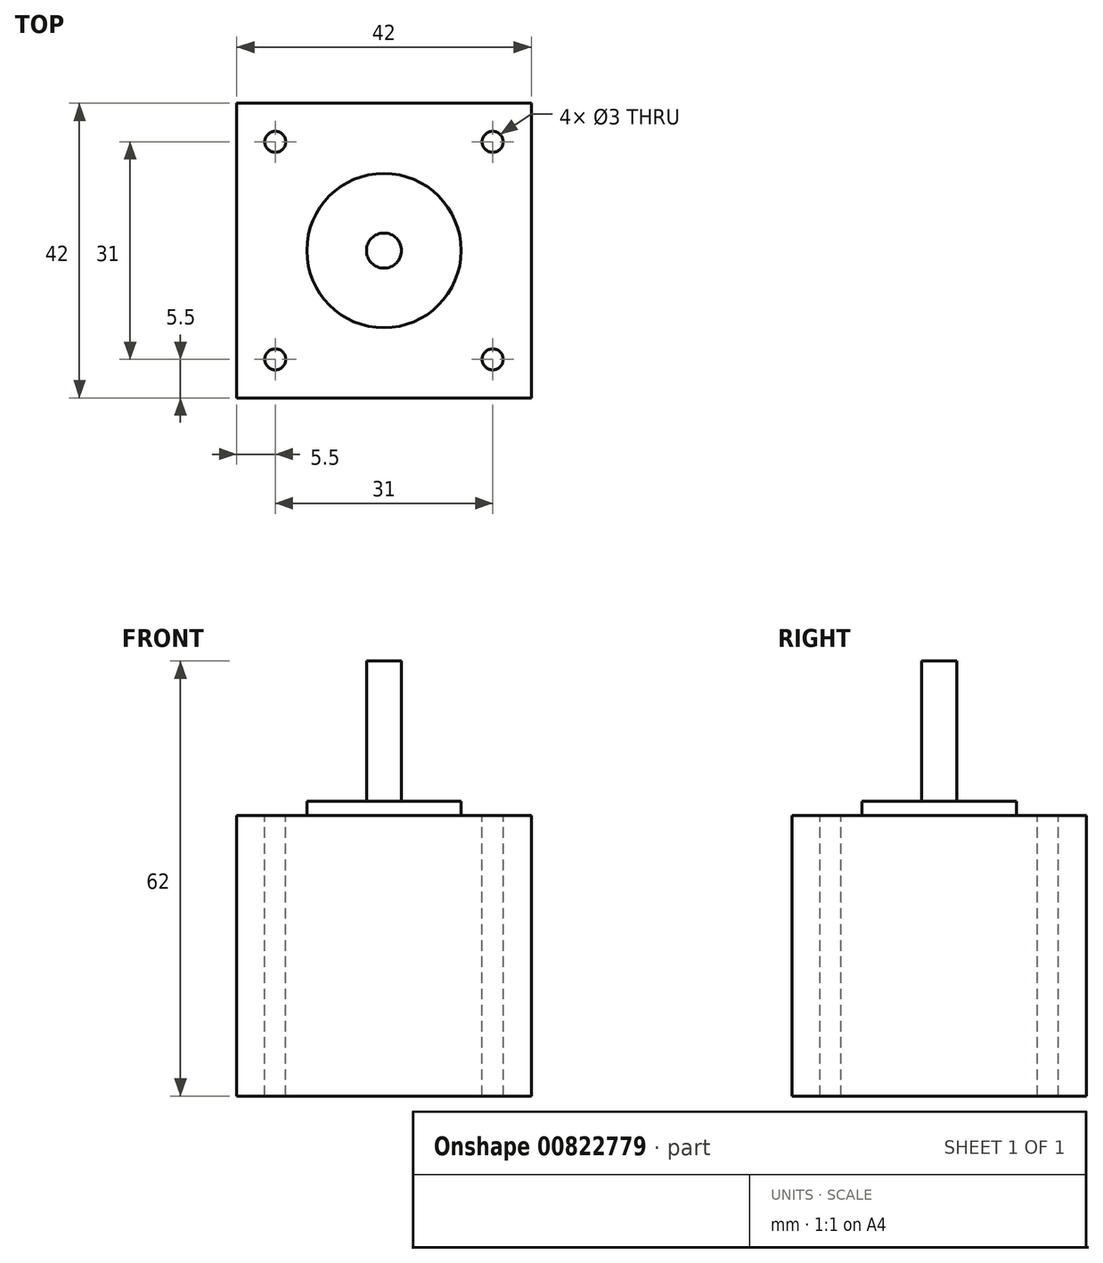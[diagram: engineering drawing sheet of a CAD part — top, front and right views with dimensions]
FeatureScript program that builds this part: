
annotation { "Feature Type Name" : "Feature", "Feature Type Description" : "" }
export const myFeature = defineFeature(function(context is Context, id is Id, definition is map)
    precondition{}
    {
        {
            var Q0;
            Q0=qCreatedBy(makeId("Top.planeOp"),FACE);
            var sketch = newSketch(context, id + "F0", { "sketchPlane" : qUnion([Q0])});
            skLineSegment(sketch, "E0.bottom", {"start": v(-21, 21) * mm, "end": v(21, 21) * mm});
            skLineSegment(sketch, "E0.top", {"start": v(-21, -21) * mm, "end": v(21, -21) * mm});
            skLineSegment(sketch, "E0.left", {"start": v(21, 21) * mm, "end": v(21, -21) * mm});
            skLineSegment(sketch, "E0.right", {"start": v(-21, 21) * mm, "end": v(-21, -21) * mm});
            skCircle(sketch, "E1", {"center": v(0, 0) * mm, "radius": 21 * mm, "construction": true});
            skLineSegment(sketch, "E2.bottom", {"start": v(15.5, 15.5) * mm, "end": v(-15.5, 15.5) * mm, "construction": true});
            skLineSegment(sketch, "E2.top", {"start": v(15.5, -15.5) * mm, "end": v(-15.5, -15.5) * mm, "construction": true});
            skLineSegment(sketch, "E2.left", {"start": v(15.5, 15.5) * mm, "end": v(15.5, -15.5) * mm, "construction": true});
            skLineSegment(sketch, "E2.right", {"start": v(-15.5, 15.5) * mm, "end": v(-15.5, -15.5) * mm, "construction": true});
            skCircle(sketch, "E3", {"center": v(-15.5, 15.5) * mm, "radius": 1.5 * mm, "construction": true});
            skCircle(sketch, "E4", {"center": v(15.5, 15.5) * mm, "radius": 1.5 * mm, "construction": true});
            skCircle(sketch, "E5", {"center": v(15.5, -15.5) * mm, "radius": 1.5 * mm, "construction": true});
            skCircle(sketch, "E6", {"center": v(-15.5, -15.5) * mm, "radius": 1.5 * mm, "construction": true});
            skCircle(sketch, "E7", {"center": v(0, 0) * mm, "radius": 11 * mm, "construction": true});
            skSolve(sketch);
        }
        {
            var Q0;
            Q0=makeQuery(id+"F0.imprint","IMPRINT",FACE,{"disambiguationData":[TD([[makeQuery(id+"F0.imprint","IMPRINT",EDGE,{"derivedFrom":sQuery(id+"F0.wireOp",EDGE,"E0.bottom")}),-1.0]])]});
            extrude(context, id + "F1", {"entities" : qUnion([Q0]), "oppositeDirection" : true, "depth" : 40 * mm, "offsetDistance" : 25 * mm});
        }
        {
            var Q0;
            Q0=makeQuery(id+"F1.opExtrude","CAP_FACE",FACE,{"disambiguationData":[OSD([sQuery(id+"F0.wireOp",EDGE,"E0.bottom"),sQuery(id+"F0.wireOp",EDGE,"E0.top"),sQuery(id+"F0.wireOp",EDGE,"E0.left"),sQuery(id+"F0.wireOp",EDGE,"E0.right"),sQuery(id+"F0.wireOp",EDGE,"E3"),sQuery(id+"F0.wireOp",EDGE,"E4"),sQuery(id+"F0.wireOp",EDGE,"E5"),sQuery(id+"F0.wireOp",EDGE,"E6")])],"isStart":true});
            var sketch = newSketch(context, id + "F2", { "sketchPlane" : qUnion([Q0])});
            skCircle(sketch, "E8.0", {"center": v(0, 0) * mm, "radius": 11 * mm});
            skSolve(sketch);
        }
        {
            var Q0;
            Q0 = qSketchRegion(id + "F2", true);
            extrude(context, id + "F3", {"entities" : qUnion([Q0]), "operationType" : NewBodyOperationType.ADD, "depth" : 2 * mm, "offsetDistance" : 25 * mm});
        }
        {
            var Q0;
            Q0=makeQuery(id+"F3.opExtrude","CAP_FACE",FACE,{"disambiguationData":[OSD([sQuery(id+"F2.wireOp",EDGE,"E8.0")])],"isStart":false});
            var sketch = newSketch(context, id + "F4", { "sketchPlane" : qUnion([Q0])});
            skPoint(sketch, "E9.0", {"position": v(0, 0) * mm});
            skCircle(sketch, "E10", {"center": v(0, 0) * mm, "radius": 2.5 * mm});
            skSolve(sketch);
        }
        {
            var Q0;
            Q0=makeQuery(id+"F4.imprint","IMPRINT",FACE,{"disambiguationData":[TD([[makeQuery(id+"F4.imprint","IMPRINT",EDGE,{"derivedFrom":sQuery(id+"F4.wireOp",EDGE,"E10")}),1.0]])]});
            extrude(context, id + "F5", {"entities" : qUnion([Q0]), "operationType" : NewBodyOperationType.ADD, "depth" : 20 * mm, "offsetDistance" : 25 * mm});
        }
        {
            var Q0;
            Q0=makeQuery(id+"F0.imprint","IMPRINT",FACE,{"disambiguationData":[TD([[makeQuery(id+"F0.imprint","IMPRINT",EDGE,{"derivedFrom":sQuery(id+"F0.wireOp",EDGE,"E0.bottom")}),-1.0]])]});
            var sketch = newSketch(context, id + "F6", { "sketchPlane" : qUnion([Q0])});
            skCircle(sketch, "E11.0", {"center": v(15.5, -15.5) * mm, "radius": 1.5 * mm});
            skCircle(sketch, "E12.0", {"center": v(15.5, 15.5) * mm, "radius": 1.5 * mm});
            skCircle(sketch, "E13.0", {"center": v(-15.5, 15.5) * mm, "radius": 1.5 * mm});
            skCircle(sketch, "E14.0", {"center": v(-15.5, -15.5) * mm, "radius": 1.5 * mm});
            skSolve(sketch);
        }
        {
            var Q0;
            Q0=makeQuery(id+"F6.imprint","IMPRINT",FACE,{"disambiguationData":[TD([[makeQuery(id+"F6.imprint","IMPRINT",EDGE,{"derivedFrom":sQuery(id+"F6.wireOp",EDGE,"E12.0")}),1.0]])]});
            var Q1;
            Q1=makeQuery(id+"F6.imprint","IMPRINT",FACE,{"disambiguationData":[TD([[makeQuery(id+"F6.imprint","IMPRINT",EDGE,{"derivedFrom":sQuery(id+"F6.wireOp",EDGE,"E13.0")}),1.0]])]});
            var Q2;
            Q2=makeQuery(id+"F6.imprint","IMPRINT",FACE,{"disambiguationData":[TD([[makeQuery(id+"F6.imprint","IMPRINT",EDGE,{"derivedFrom":sQuery(id+"F6.wireOp",EDGE,"E14.0")}),1.0]])]});
            var Q3;
            Q3=makeQuery(id+"F6.imprint","IMPRINT",FACE,{"disambiguationData":[TD([[makeQuery(id+"F6.imprint","IMPRINT",EDGE,{"derivedFrom":sQuery(id+"F6.wireOp",EDGE,"E11.0")}),1.0]])]});
            extrude(context, id + "F7", {"entities" : qUnion([Q0, Q1, Q2, Q3]), "operationType" : NewBodyOperationType.REMOVE, "endBound" : BoundingType.THROUGH_ALL, "oppositeDirection" : true, "depth" : 25 * mm, "offsetDistance" : 25 * mm});
        }
    });
